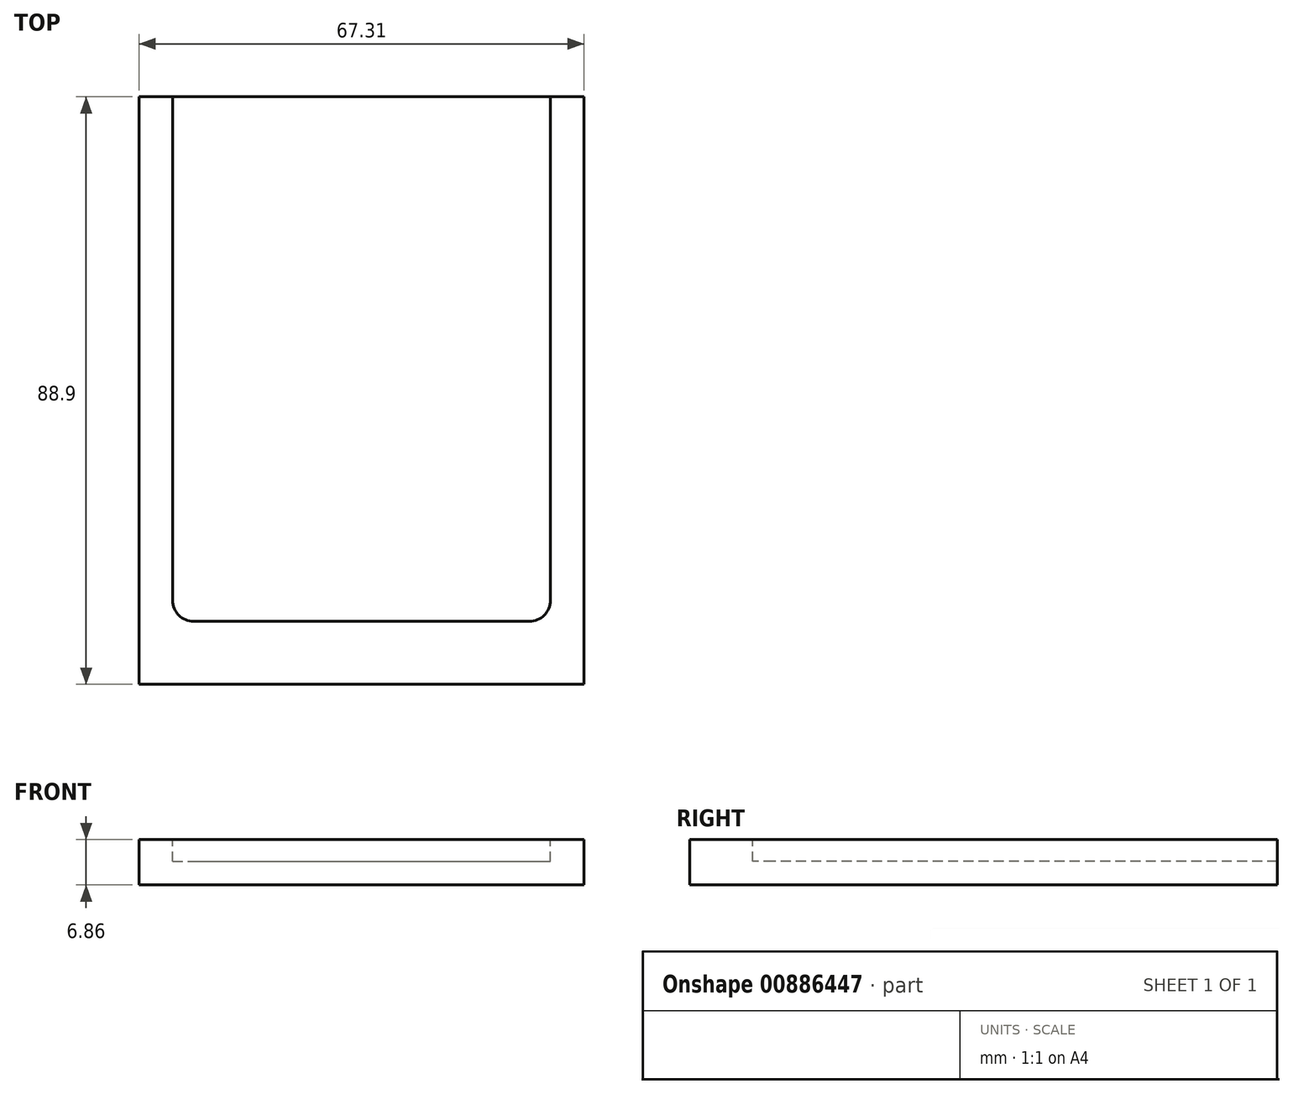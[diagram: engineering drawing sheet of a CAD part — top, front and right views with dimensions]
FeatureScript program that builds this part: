
annotation { "Feature Type Name" : "Feature", "Feature Type Description" : "" }
export const myFeature = defineFeature(function(context is Context, id is Id, definition is map)
    precondition{}
    {
        {
            var Q0;
            Q0=qCreatedBy(makeId("Top.planeOp"),FACE);
            var sketch = newSketch(context, id + "F0", { "sketchPlane" : qUnion([Q0])});
            skLineSegment(sketch, "E0.bottom", {"start": v(-67.31, 117.07) * mm, "end": v(0, 117.07) * mm});
            skLineSegment(sketch, "E0.top", {"start": v(-67.31, 28.17) * mm, "end": v(0, 28.17) * mm});
            skLineSegment(sketch, "E0.left", {"start": v(-67.31, 117.07) * mm, "end": v(-67.31, 28.17) * mm});
            skLineSegment(sketch, "E0.right", {"start": v(0, 117.07) * mm, "end": v(0, 28.17) * mm});
            skSolve(sketch);
        }
        {
            var Q0;
            Q0=makeQuery(id+"F0.imprint","IMPRINT",FACE,{"disambiguationData":[TD([[makeQuery(id+"F0.imprint","IMPRINT",EDGE,{"derivedFrom":sQuery(id+"F0.wireOp",EDGE,"E0.bottom")}),-1.0]])]});
            extrude(context, id + "F1", {"entities" : qUnion([Q0]), "depth" : 6.86 * mm, "offsetDistance" : 25.4 * mm});
        }
        {
            var Q0;
            Q0=makeQuery(id+"F1.opExtrude","CAP_FACE",FACE,{"disambiguationData":[OSD([sQuery(id+"F0.wireOp",EDGE,"E0.bottom"),sQuery(id+"F0.wireOp",EDGE,"E0.top"),sQuery(id+"F0.wireOp",EDGE,"E0.left"),sQuery(id+"F0.wireOp",EDGE,"E0.right")])],"isStart":false});
            var sketch = newSketch(context, id + "F2", { "sketchPlane" : qUnion([Q0])});
            skLineSegment(sketch, "E1.bottom", {"start": v(-62.23, 117.07) * mm, "end": v(-5.08, 117.07) * mm});
            skLineSegment(sketch, "E1.top", {"start": v(-59.05, 37.7) * mm, "end": v(-8.26, 37.7) * mm});
            skLineSegment(sketch, "E1.left", {"start": v(-62.23, 117.07) * mm, "end": v(-62.23, 40.87) * mm});
            skLineSegment(sketch, "E1.right", {"start": v(-5.08, 117.07) * mm, "end": v(-5.08, 40.87) * mm});
            skPoint(sketch, "E2.visualSharp", {"position": v(-62.23, 37.7) * mm});
            skArc(sketch, "E2.filletArc", {"start": v(-62.23, 40.87) * mm, "mid": v(-61.3, 38.62) * mm, "end": v(-59.05, 37.7) * mm});
            skPoint(sketch, "E3.visualSharp", {"position": v(-5.08, 37.7) * mm});
            skArc(sketch, "E3.filletArc", {"start": v(-8.26, 37.7) * mm, "mid": v(-6, 38.62) * mm, "end": v(-5.08, 40.87) * mm});
            skSolve(sketch);
        }
        {
            var Q0;
            Q0=makeQuery(id+"F2.imprint","IMPRINT",FACE,{"disambiguationData":[TD([[makeQuery(id+"F2.imprint","IMPRINT",EDGE,{"derivedFrom":sQuery(id+"F2.wireOp",EDGE,"E1.bottom")}),-1.0]])]});
            extrude(context, id + "F3", {"entities" : qUnion([Q0]), "operationType" : NewBodyOperationType.REMOVE, "oppositeDirection" : true, "depth" : 3.3 * mm, "offsetDistance" : 25.4 * mm});
        }
    });
